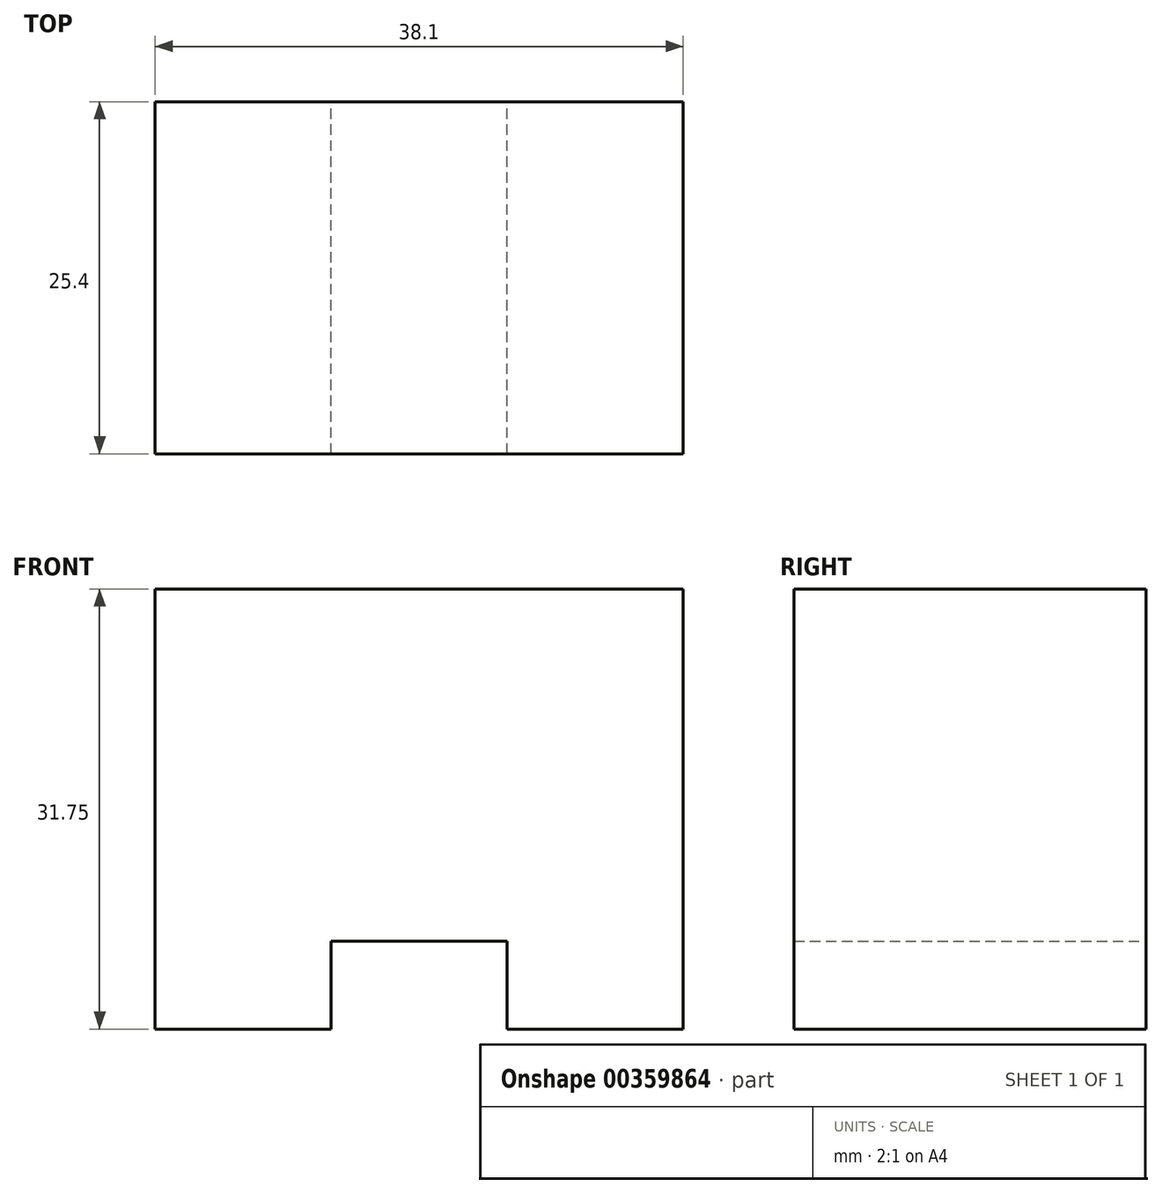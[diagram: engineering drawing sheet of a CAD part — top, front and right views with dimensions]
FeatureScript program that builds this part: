
annotation { "Feature Type Name" : "Feature", "Feature Type Description" : "" }
export const myFeature = defineFeature(function(context is Context, id is Id, definition is map)
    precondition{}
    {
        {
            var Q0;
            Q0=qCreatedBy(makeId("Front.planeOp"),FACE);
            var sketch = newSketch(context, id + "F0", { "sketchPlane" : qUnion([Q0])});
            skLineSegment(sketch, "E0", {"start": v(0, 0) * mm, "end": v(12.7, 0) * mm});
            skLineSegment(sketch, "E1", {"start": v(12.7, 0) * mm, "end": v(12.7, 6.35) * mm});
            skLineSegment(sketch, "E2", {"start": v(12.7, 6.35) * mm, "end": v(25.4, 6.35) * mm});
            skLineSegment(sketch, "E3", {"start": v(25.4, 6.35) * mm, "end": v(25.4, 0) * mm});
            skLineSegment(sketch, "E4", {"start": v(25.4, 0) * mm, "end": v(38.1, 0) * mm});
            skLineSegment(sketch, "E5", {"start": v(38.1, 0) * mm, "end": v(38.1, 31.75) * mm});
            skLineSegment(sketch, "E6", {"start": v(38.1, 31.75) * mm, "end": v(0, 31.75) * mm});
            skLineSegment(sketch, "E7", {"start": v(0, 31.75) * mm, "end": v(0, 0) * mm});
            skSolve(sketch);
        }
        {
            var Q0;
            Q0=makeQuery(id+"F0.imprint","IMPRINT",FACE,{"disambiguationData":[TD([[makeQuery(id+"F0.imprint","IMPRINT",EDGE,{"derivedFrom":sQuery(id+"F0.wireOp",EDGE,"E0")}),1.0]])]});
            extrude(context, id + "F1", {"entities" : qUnion([Q0]), "depth" : 25.4 * mm});
        }
    });
